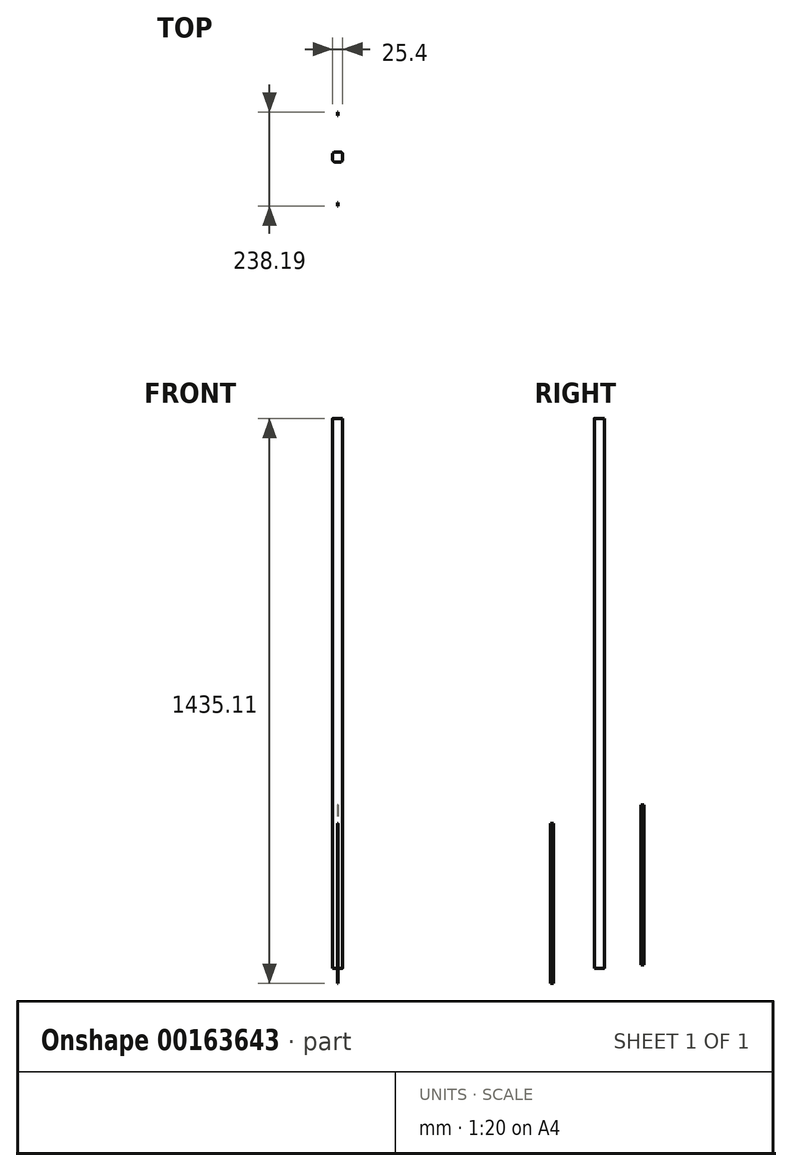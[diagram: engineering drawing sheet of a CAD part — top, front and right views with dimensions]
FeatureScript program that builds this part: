
annotation { "Feature Type Name" : "Feature", "Feature Type Description" : "" }
export const myFeature = defineFeature(function(context is Context, id is Id, definition is map)
    precondition{}
    {
        {
            var Q0;
            Q0=qCreatedBy(makeId("Top.planeOp"),FACE);
            var sketch = newSketch(context, id + "F0", { "sketchPlane" : qUnion([Q0])});
            skLineSegment(sketch, "E0.bottom", {"start": v(6.35, 12.7) * mm, "end": v(-6.35, 12.7) * mm});
            skLineSegment(sketch, "E0.top", {"start": v(6.35, -12.7) * mm, "end": v(-6.35, -12.7) * mm});
            skLineSegment(sketch, "E0.left", {"start": v(12.7, 6.35) * mm, "end": v(12.7, -6.35) * mm});
            skLineSegment(sketch, "E0.right", {"start": v(-12.7, 6.35) * mm, "end": v(-12.7, -6.35) * mm});
            skPoint(sketch, "E0.middle", {"position": v(0, 0) * mm});
            skPoint(sketch, "E1.visualSharp", {"position": v(-12.7, 12.7) * mm});
            skArc(sketch, "E1.filletArc", {"start": v(-6.35, 12.7) * mm, "mid": v(-10.84, 10.84) * mm, "end": v(-12.7, 6.35) * mm});
            skPoint(sketch, "E2.visualSharp", {"position": v(-12.7, -12.7) * mm});
            skArc(sketch, "E2.filletArc", {"start": v(-12.7, -6.35) * mm, "mid": v(-10.84, -10.84) * mm, "end": v(-6.35, -12.7) * mm});
            skPoint(sketch, "E3.visualSharp", {"position": v(12.7, -12.7) * mm});
            skArc(sketch, "E3.filletArc", {"start": v(6.35, -12.7) * mm, "mid": v(10.84, -10.84) * mm, "end": v(12.7, -6.35) * mm});
            skPoint(sketch, "E4.visualSharp", {"position": v(12.7, 12.7) * mm});
            skArc(sketch, "E4.filletArc", {"start": v(12.7, 6.35) * mm, "mid": v(10.84, 10.84) * mm, "end": v(6.35, 12.7) * mm});
            skSolve(sketch);
        }
        {
            var Q0;
            Q0=qSketchRegion(id+"F0",true);
            extrude(context, id + "F1", {"entities" : qUnion([Q0]), "depth" : 1397 * mm, "offsetDistance" : 25.4 * mm});
        }
        {
            var Q0;
            Q0=qCreatedBy(makeId("Right.planeOp"),FACE);
            var sketch = newSketch(context, id + "F2", { "sketchPlane" : qUnion([Q0])});
            skLineSegment(sketch, "E5.bottom", {"start": v(-124.27, 368.3) * mm, "end": v(-115.8, 368.3) * mm});
            skLineSegment(sketch, "E5.top", {"start": v(-124.27, -38.1) * mm, "end": v(-115.8, -38.1) * mm});
            skLineSegment(sketch, "E5.left", {"start": v(-124.27, 368.3) * mm, "end": v(-124.27, -38.1) * mm});
            skLineSegment(sketch, "E5.right", {"start": v(-115.8, 368.3) * mm, "end": v(-115.8, -38.1) * mm});
            skSolve(sketch);
        }
        {
            var Q0;
            Q0=makeQuery(id+"F2.imprint","IMPRINT",FACE,{"disambiguationData":[TD([[makeQuery(id+"F2.imprint","IMPRINT",EDGE,{"derivedFrom":sQuery(id+"F2.wireOp",EDGE,"E5.bottom")}),-1.0]])]});
            extrude(context, id + "F3", {"entities" : qUnion([Q0]), "depth" : 1.27 * mm});
        }
        {
            var Q0;
            Q0=qCreatedBy(makeId("Right.planeOp"),FACE);
            var sketch = newSketch(context, id + "F4", { "sketchPlane" : qUnion([Q0])});
            skLineSegment(sketch, "E6.bottom", {"start": v(105.46, 415.6) * mm, "end": v(113.92, 415.6) * mm});
            skLineSegment(sketch, "E6.top", {"start": v(105.46, 9.2) * mm, "end": v(113.92, 9.2) * mm});
            skLineSegment(sketch, "E6.left", {"start": v(105.46, 415.6) * mm, "end": v(105.46, 9.2) * mm});
            skLineSegment(sketch, "E6.right", {"start": v(113.92, 415.6) * mm, "end": v(113.92, 9.2) * mm});
            skSolve(sketch);
        }
        {
            var Q0;
            Q0=makeQuery(id+"F4.imprint","IMPRINT",FACE,{"disambiguationData":[TD([[makeQuery(id+"F4.imprint","IMPRINT",EDGE,{"derivedFrom":sQuery(id+"F4.wireOp",EDGE,"E6.bottom")}),-1.0]])]});
            extrude(context, id + "F5", {"entities" : qUnion([Q0]), "depth" : 1.27 * mm});
        }
    });
